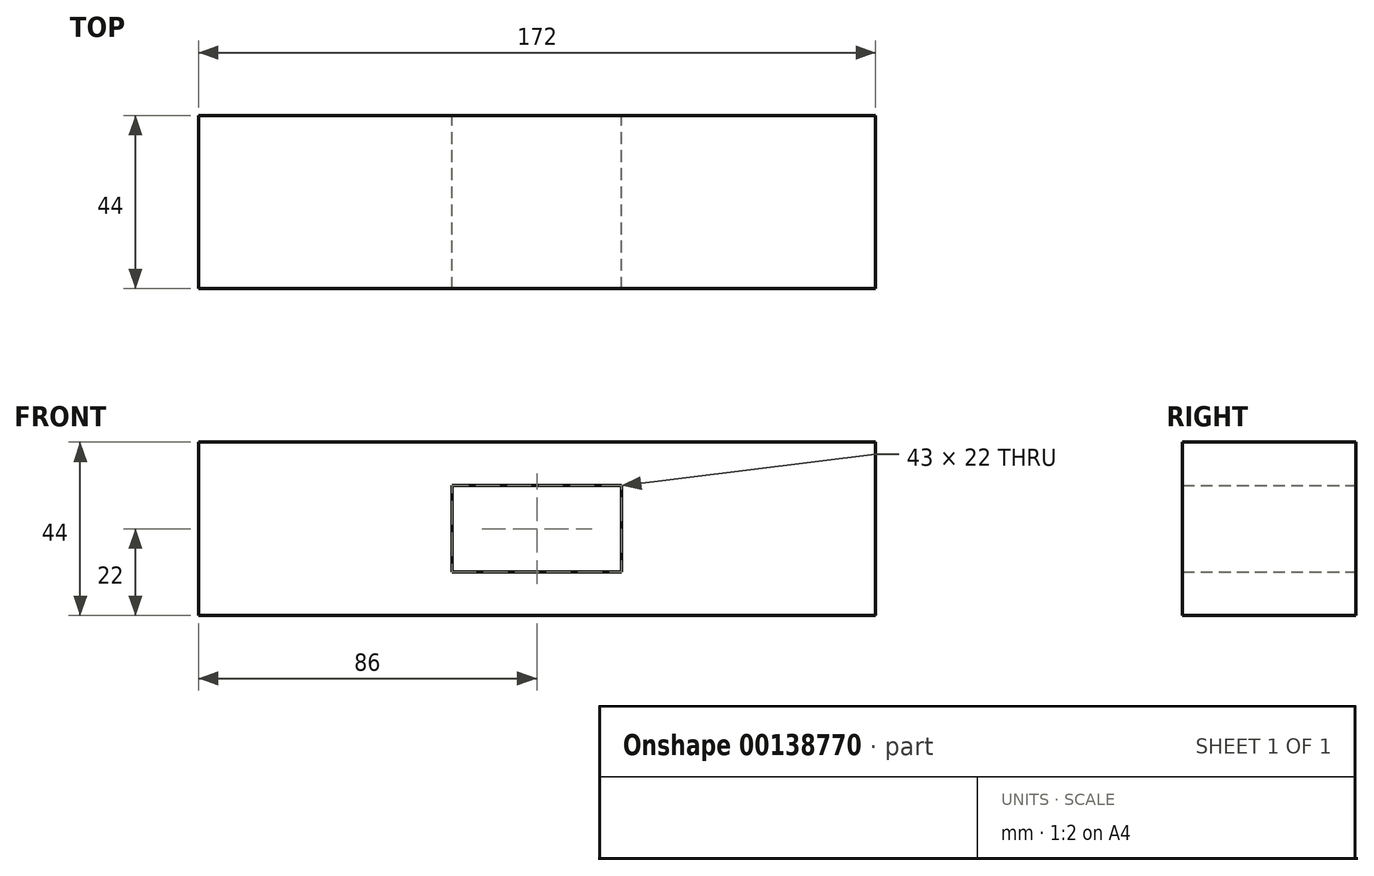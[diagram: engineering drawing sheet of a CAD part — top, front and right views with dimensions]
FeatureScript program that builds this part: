
annotation { "Feature Type Name" : "Feature", "Feature Type Description" : "" }
export const myFeature = defineFeature(function(context is Context, id is Id, definition is map)
    precondition{}
    {
        {
            var Q0;
            Q0=qCreatedBy(makeId("Front.planeOp"),FACE);
            var sketch = newSketch(context, id + "F0", { "sketchPlane" : qUnion([Q0])});
            skLineSegment(sketch, "E0.bottom", {"start": v(86, 22) * mm, "end": v(-86, 22) * mm});
            skLineSegment(sketch, "E0.top", {"start": v(86, -22) * mm, "end": v(-86, -22) * mm});
            skLineSegment(sketch, "E0.left", {"start": v(86, 22) * mm, "end": v(86, -22) * mm});
            skLineSegment(sketch, "E0.right", {"start": v(-86, 22) * mm, "end": v(-86, -22) * mm});
            skPoint(sketch, "E0.middle", {"position": v(0, 0) * mm});
            skLineSegment(sketch, "E1.bottom", {"start": v(21.5, 11) * mm, "end": v(-21.5, 11) * mm});
            skLineSegment(sketch, "E1.top", {"start": v(21.5, -11) * mm, "end": v(-21.5, -11) * mm});
            skLineSegment(sketch, "E1.left", {"start": v(21.5, 11) * mm, "end": v(21.5, -11) * mm});
            skLineSegment(sketch, "E1.right", {"start": v(-21.5, 11) * mm, "end": v(-21.5, -11) * mm});
            skSolve(sketch);
        }
        {
            var Q0;
            Q0=makeQuery(id+"F0.imprint","IMPRINT",FACE,{"disambiguationData":[TD([[makeQuery(id+"F0.imprint","IMPRINT",EDGE,{"derivedFrom":sQuery(id+"F0.wireOp",EDGE,"E0.bottom")}),1.0]])]});
            extrude(context, id + "F1", {"entities" : qUnion([Q0]), "endBound" : BoundingType.SYMMETRIC, "depth" : 44 * mm});
        }
    });
